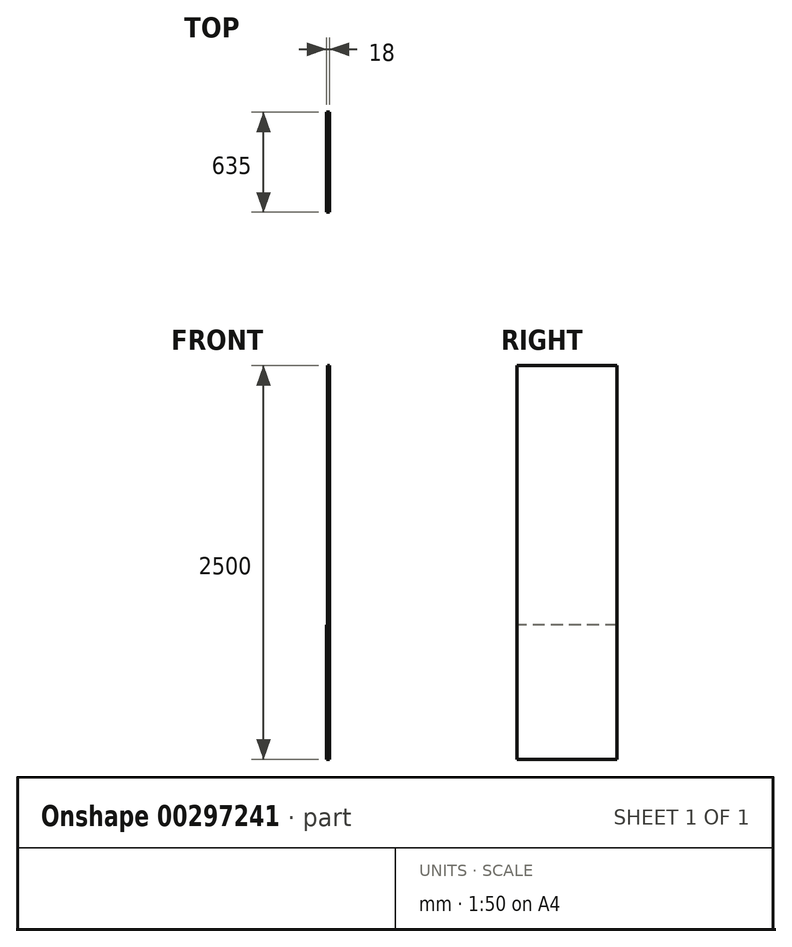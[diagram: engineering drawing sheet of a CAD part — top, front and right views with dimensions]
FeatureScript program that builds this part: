
annotation { "Feature Type Name" : "Feature", "Feature Type Description" : "" }
export const myFeature = defineFeature(function(context is Context, id is Id, definition is map)
    precondition{}
    {
        {
            var Q0;
            Q0=qCreatedBy(makeId("Right.planeOp"),FACE);
            var sketch = newSketch(context, id + "F0", { "sketchPlane" : qUnion([Q0])});
            skLineSegment(sketch, "E0.bottom", {"start": v(317.5, 1250) * mm, "end": v(-317.5, 1250) * mm});
            skLineSegment(sketch, "E0.top", {"start": v(317.5, -1250) * mm, "end": v(-317.5, -1250) * mm});
            skLineSegment(sketch, "E0.left", {"start": v(317.5, 1250) * mm, "end": v(317.5, -1250) * mm});
            skLineSegment(sketch, "E0.right", {"start": v(-317.5, 1250) * mm, "end": v(-317.5, -1250) * mm});
            skPoint(sketch, "E0.middle", {"position": v(0, 0) * mm});
            skSolve(sketch);
        }
        {
            var Q0;
            Q0=makeQuery(id+"F0.imprint","IMPRINT",FACE,{"disambiguationData":[TD([[makeQuery(id+"F0.imprint","IMPRINT",EDGE,{"derivedFrom":sQuery(id+"F0.wireOp",EDGE,"E0.bottom")}),1.0]])]});
            extrude(context, id + "F1", {"entities" : qUnion([Q0]), "depth" : 18 * mm});
        }
        {
            var Q0;
            Q0=makeQuery(id+"F1.opExtrude","CAP_FACE",FACE,{"disambiguationData":[OSD([sQuery(id+"F0.wireOp",EDGE,"E0.bottom"),sQuery(id+"F0.wireOp",EDGE,"E0.top"),sQuery(id+"F0.wireOp",EDGE,"E0.left"),sQuery(id+"F0.wireOp",EDGE,"E0.right")])],"isStart":true});
            var sketch = newSketch(context, id + "F2", { "sketchPlane" : qUnion([Q0])});
            skLineSegment(sketch, "E1.bottom", {"start": v(-317.5, 1250) * mm, "end": v(317.5, 1250) * mm});
            skLineSegment(sketch, "E1.top", {"start": v(-317.5, -398) * mm, "end": v(317.5, -398) * mm});
            skLineSegment(sketch, "E1.left", {"start": v(-317.5, 1250) * mm, "end": v(-317.5, -398) * mm});
            skLineSegment(sketch, "E1.right", {"start": v(317.5, 1250) * mm, "end": v(317.5, -398) * mm});
            skSolve(sketch);
        }
        {
            var Q0;
            Q0 = qSketchRegion(id + "F2", true);
            extrude(context, id + "F3", {"entities" : qUnion([Q0]), "operationType" : NewBodyOperationType.REMOVE, "oppositeDirection" : true, "depth" : 6 * mm});
        }
    });
